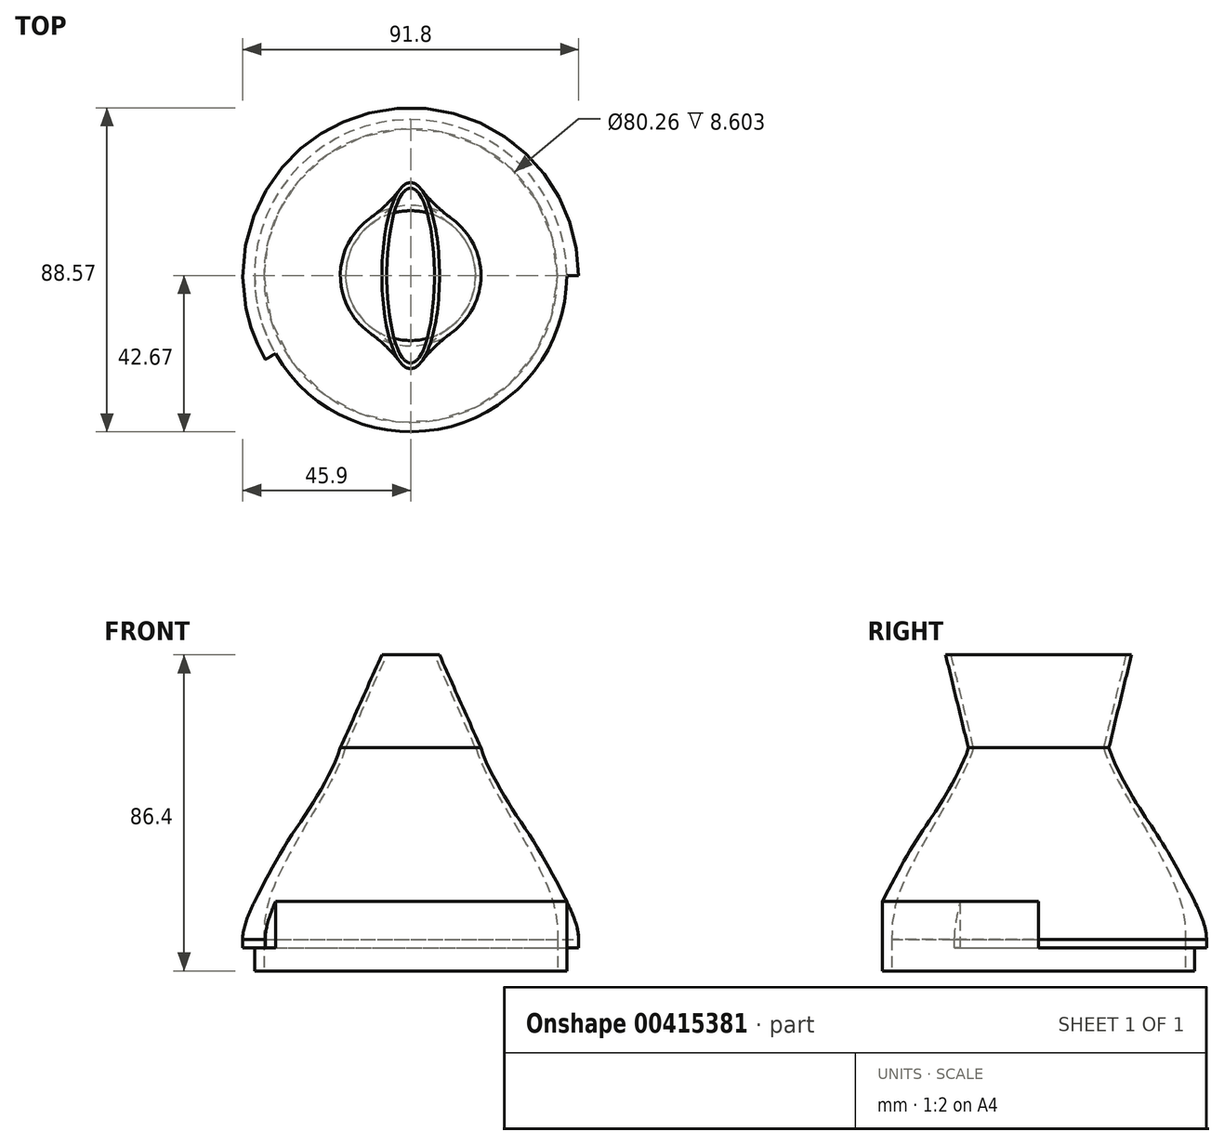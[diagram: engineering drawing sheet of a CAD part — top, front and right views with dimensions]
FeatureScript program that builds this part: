
annotation { "Feature Type Name" : "Feature", "Feature Type Description" : "" }
export const myFeature = defineFeature(function(context is Context, id is Id, definition is map)
    precondition{}
    {
        {
            var Q0;
            Q0=qCreatedBy(makeId("Front.planeOp"),FACE);
            var sketch = newSketch(context, id + "F0", { "sketchPlane" : qUnion([Q0])});
            skLineSegment(sketch, "E0", {"start": v(42.67, 0) * mm, "end": v(42.67, -6.35) * mm});
            skLineSegment(sketch, "E1", {"start": v(42.67, -6.35) * mm, "end": v(40.13, -6.35) * mm});
            skLineSegment(sketch, "E2", {"start": v(40.13, -6.35) * mm, "end": v(40.13, 0) * mm});
            skLineSegment(sketch, "E3.bottom", {"start": v(40.13, 0) * mm, "end": v(45.9, 0) * mm});
            skLineSegment(sketch, "E3.top", {"start": v(40.13, 2.25) * mm, "end": v(45.9, 2.25) * mm});
            skLineSegment(sketch, "E3.left", {"start": v(40.13, 0) * mm, "end": v(40.13, 2.25) * mm});
            skLineSegment(sketch, "E3.right", {"start": v(45.9, 0) * mm, "end": v(45.9, 2.25) * mm});
            skFitSpline(sketch, "E4", {"points": [v(40.13, 2.25) * mm, v(37.64, 16.16) * mm, v(24.94, 39.83) * mm, v(17.8, 54.65) * mm], "startDerivative": vector(1.2, 47.39) * mm, "endDerivative": vector(-11.04, 38.55) * mm});
            skFitSpline(sketch, "E5", {"points": [v(45.9, 2.25) * mm, v(40.74, 16.38) * mm, v(33.56, 29.1) * mm, v(25.7, 41.24) * mm, v(19.2, 54.65) * mm], "startDerivative": vector(1.2, 47.39) * mm, "endDerivative": vector(-11.06, 39.62) * mm});
            skLineSegment(sketch, "E6", {"start": v(17.8, 54.65) * mm, "end": v(19.2, 54.65) * mm});
            skLineSegment(sketch, "E7", {"start": v(42.67, 0) * mm, "end": v(42.67, 2.25) * mm});
            skPoint(sketch, "E7.endSnap0", {"position": v(43.02, 2.25) * mm});
            skLineSegment(sketch, "E8", {"start": v(42.67, 2.25) * mm, "end": v(42.67, 12.6) * mm});
            skSolve(sketch);
        }
        {
            var Q0;
            Q0=qCreatedBy(makeId("Front.planeOp"),FACE);
            var sketch = newSketch(context, id + "F1", { "sketchPlane" : qUnion([Q0])});
            skLineSegment(sketch, "E9", {"start": v(0, 0) * mm, "end": v(0, 103.56) * mm});
            skLineSegment(sketch, "E10", {"start": v(0, 103.56) * mm, "end": v(13.59, 103.56) * mm});
            skSolve(sketch);
        }
        {
            var Q0;
            Q0 = qSketchRegion(id + "F0", true);
            var Q1;
            Q1=sQuery(id+"F1.wireOp",EDGE,"E9");
            revolve(context, id + "F2", {"entities" : qUnion([Q0]), "axis" : qUnion([Q1]), "revolveType" : RevolveType.ONE_DIRECTION, "angle" : 210 * degree});
        }
        {
            var Q0;
            {var subQ3=sQuery(id+"F0.wireOp",EDGE,"E4");Q0=makeQuery(id+"F0.imprint","IMPRINT",FACE,{"disambiguationData":[TD([[makeQuery(id+"F0.imprint","IMPRINT",EDGE,{"derivedFrom":subQ3}),-1.0]])]});}
            var Q1;
            {var subQ2=sQuery(id+"F0.wireOp",EDGE,"E3.left");Q1=makeQuery(id+"F0.imprint","IMPRINT",FACE,{"disambiguationData":[TD([[makeQuery(id+"F0.imprint","IMPRINT",EDGE,{"derivedFrom":subQ2}),-1.0]])]});}
            var Q2;
            {var subQ0=sQuery(id+"F0.wireOp",EDGE,"E0");Q2=makeQuery(id+"F0.imprint","IMPRINT",FACE,{"disambiguationData":[TD([[makeQuery(id+"F0.imprint","IMPRINT",EDGE,{"derivedFrom":subQ0}),-1.0]])]});}
            var Q3;
            Q3=sQuery(id+"F1.wireOp",EDGE,"E9");
            revolve(context, id + "F3", {"operationType" : NewBodyOperationType.ADD, "entities" : qUnion([Q0, Q1, Q2]), "axis" : qUnion([Q3]), "revolveType" : RevolveType.ONE_DIRECTION, "oppositeDirection" : true, "angle" : 150 * degree});
        }
        {
            var Q0;
            {var subQ0=sQuery(id+"F0.wireOp",EDGE,"E6");Q0=makeQuery(id+"F3.boolean.opBoolean","MERGE",FACE,{"derivedFrom":[makeQuery(id+"F2.opRevolve","SWEPT_FACE",FACE,{"disambiguationData":[OSD([subQ0])]}),makeQuery(id+"F3.opRevolve","SWEPT_FACE",FACE,{"disambiguationData":[OSD([subQ0])]})]});}
            cPlane(context, id + "F4", {"entities" : qUnion([Q0]), "cplaneType" : CPlaneType.OFFSET, "offset" : 25.4 * mm, "width" : 152.4 * mm, "height" : 152.4 * mm});
        }
        {
            var Q0;
            Q0=qCreatedBy(id+"F4.planeOp",FACE);
            var sketch = newSketch(context, id + "F5", { "sketchPlane" : qUnion([Q0])});
            skEllipse(sketch, "E11", {"center": v(0, 0) * mm, "majorRadius": 25.4 * mm, "minorRadius": 7.88 * mm, "majorAxis": v(0, 1)});
            skSolve(sketch);
        }
        {
            var Q0;
            {var subQ0=sQuery(id+"F0.wireOp",EDGE,"E6");Q0=makeQuery(id+"F3.boolean.opBoolean","MERGE",FACE,{"derivedFrom":[makeQuery(id+"F2.opRevolve","SWEPT_FACE",FACE,{"disambiguationData":[OSD([subQ0])]}),makeQuery(id+"F3.opRevolve","SWEPT_FACE",FACE,{"disambiguationData":[OSD([subQ0])]})]});}
            var sketch = newSketch(context, id + "F6", { "sketchPlane" : qUnion([Q0])});
            skCircle(sketch, "E12", {"center": v(0, 0) * mm, "radius": 19.2 * mm});
            skSolve(sketch);
        }
        {
            var Q1;
            Q1 = qSketchRegion(id + "F6", true);
            var Q2;
            Q2 = qSketchRegion(id + "F5", true);
            loft(context, id + "F7", {"operationType" : NewBodyOperationType.ADD, "sheetProfilesArray" : [{ "sheetProfileEntities" : qUnion([Q1]) }, { "sheetProfileEntities" : qUnion([Q2]) }]});
        }
        {
            var Q0;
            Q0=makeQuery(id+"F5.imprint","IMPRINT",FACE,{"disambiguationData":[TD([[makeQuery(id+"F5.imprint","IMPRINT",EDGE,{"derivedFrom":sQuery(id+"F5.wireOp",EDGE,"E11")}),1.0]])]});
            var sketch = newSketch(context, id + "F8", { "sketchPlane" : qUnion([Q0])});
            skEllipse(sketch, "E13", {"center": v(0, 0) * mm, "majorRadius": 23.91 * mm, "minorRadius": 6.52 * mm, "majorAxis": v(0, 1)});
            skSolve(sketch);
        }
        {
            var Q0;
            Q0=makeQuery(id+"F7.opLoft","CAP_FACE",FACE,{"disambiguationData":[OSD([makeQuery(id+"F6.imprint","IMPRINT",FACE,{"disambiguationData":[TD([[makeQuery(id+"F6.imprint","IMPRINT",EDGE,{"derivedFrom":sQuery(id+"F6.wireOp",EDGE,"E12")}),1.0]])]})])],"isStart":true});
            var sketch = newSketch(context, id + "F9", { "sketchPlane" : qUnion([Q0])});
            skCircle(sketch, "E14", {"center": v(0, 0) * mm, "radius": 17.74 * mm});
            skSolve(sketch);
        }
        {
            var Q1;
            Q1 = qSketchRegion(id + "F8", true);
            var Q2;
            Q2 = qSketchRegion(id + "F9", true);
            loft(context, id + "F10", {"operationType" : NewBodyOperationType.REMOVE, "sheetProfilesArray" : [{ "sheetProfileEntities" : qUnion([Q1]) }, { "sheetProfileEntities" : qUnion([Q2]) }]});
        }
    });
